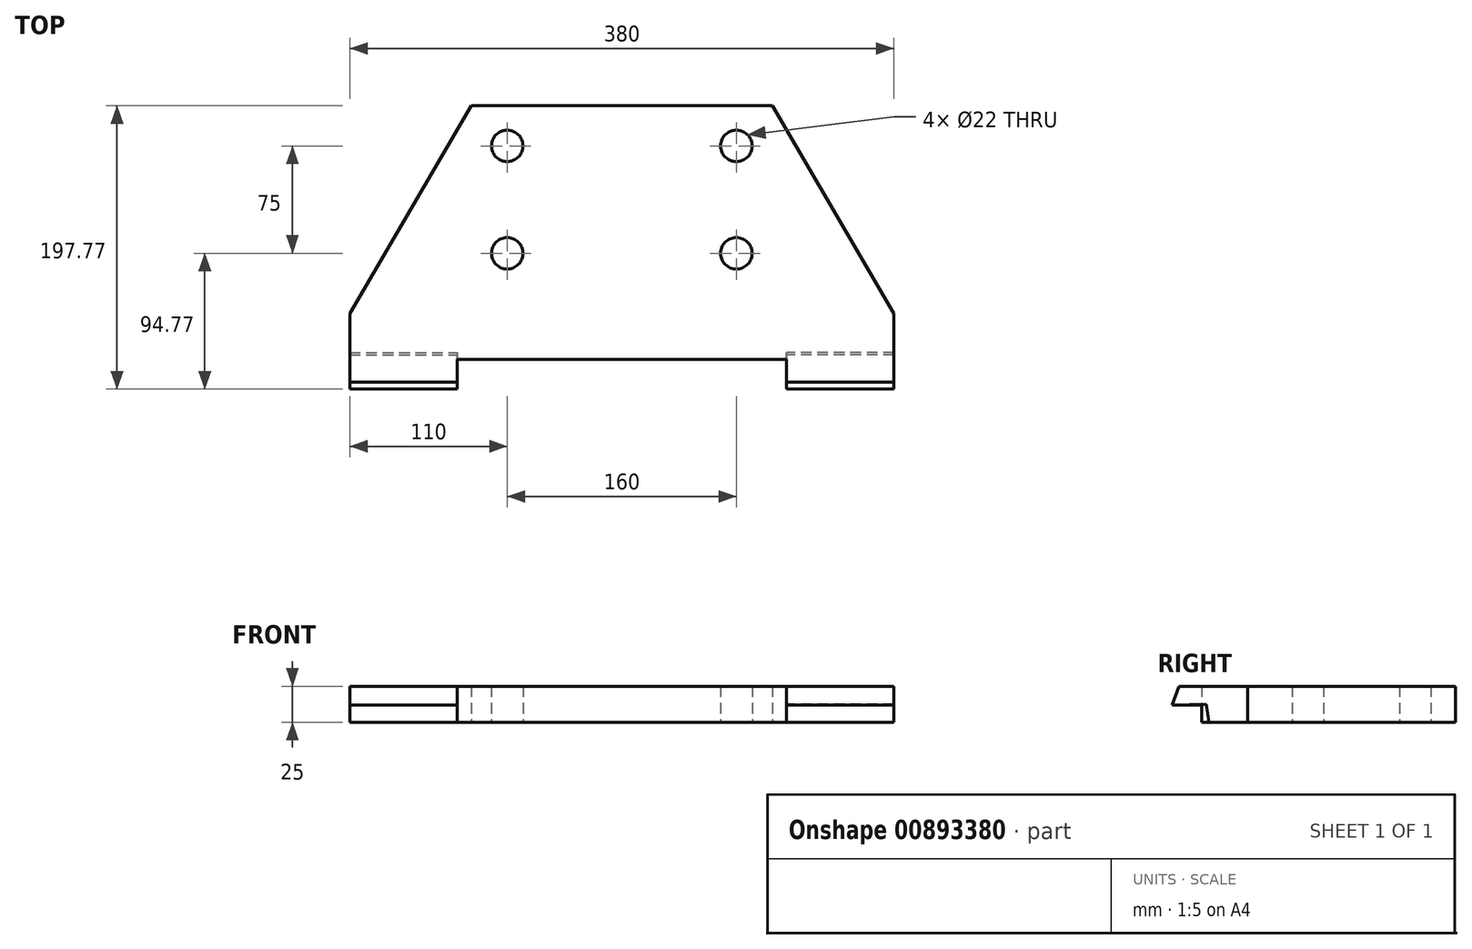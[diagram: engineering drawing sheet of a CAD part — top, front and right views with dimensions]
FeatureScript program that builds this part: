
annotation { "Feature Type Name" : "Feature", "Feature Type Description" : "" }
export const myFeature = defineFeature(function(context is Context, id is Id, definition is map)
    precondition{}
    {
        {
            var Q0;
            Q0=qCreatedBy(makeId("Top.planeOp"),FACE);
            var sketch = newSketch(context, id + "F0", { "sketchPlane" : qUnion([Q0])});
            skLineSegment(sketch, "E0", {"start": v(-105, 101) * mm, "end": v(105, 101) * mm});
            skLineSegment(sketch, "E1", {"start": v(105, 101) * mm, "end": v(190, -44) * mm});
            skLineSegment(sketch, "E2", {"start": v(190, -44) * mm, "end": v(190, -101) * mm});
            skLineSegment(sketch, "E3", {"start": v(190, -101) * mm, "end": v(115, -101) * mm});
            skLineSegment(sketch, "E4", {"start": v(115, -101) * mm, "end": v(115, -76) * mm});
            skLineSegment(sketch, "E5", {"start": v(115, -76) * mm, "end": v(-115, -76) * mm});
            skLineSegment(sketch, "E6", {"start": v(-115, -76) * mm, "end": v(-115, -101) * mm});
            skLineSegment(sketch, "E7", {"start": v(-115, -101) * mm, "end": v(-190, -101) * mm});
            skLineSegment(sketch, "E8", {"start": v(-190, -101) * mm, "end": v(-190, -44) * mm});
            skLineSegment(sketch, "E9", {"start": v(-190, -44) * mm, "end": v(-105, 101) * mm});
            skSolve(sketch);
        }
        {
            var Q0;
            Q0 = qSketchRegion(id + "F0", true);
            extrude(context, id + "F1", {"entities" : qUnion([Q0]), "depth" : 12.5 * mm, "offsetDistance" : 25.4 * mm, "hasSecondDirection" : true, "secondDirectionOppositeDirection" : true, "secondDirectionDepth" : 12.5 * mm});
        }
        {
            var Q0;
            Q0=qCreatedBy(makeId("Right.planeOp"),FACE);
            var sketch = newSketch(context, id + "F2", { "sketchPlane" : qUnion([Q0])});
            skLineSegment(sketch, "E10", {"start": v(-101, 12.5) * mm, "end": v(-92, 12.5) * mm});
            skLineSegment(sketch, "E11", {"start": v(-92, 12.5) * mm, "end": v(-101.17, -12.5) * mm});
            skLineSegment(sketch, "E12", {"start": v(-101.17, -12.5) * mm, "end": v(-101, 12.5) * mm});
            skSolve(sketch);
        }
        {
            var Q0;
            Q0=makeQuery(id+"F2.imprint","IMPRINT",FACE,{"disambiguationData":[TD([[makeQuery(id+"F2.imprint","IMPRINT",EDGE,{"derivedFrom":sQuery(id+"F2.wireOp",EDGE,"E10")}),-1.0]])]});
            extrude(context, id + "F3", {"entities" : qUnion([Q0]), "operationType" : NewBodyOperationType.REMOVE, "depth" : 190 * mm, "offsetDistance" : 25.4 * mm, "hasSecondDirection" : true, "secondDirectionOppositeDirection" : true, "secondDirectionDepth" : 190 * mm});
        }
        {
            var Q0;
            Q0=makeQuery(id+"F1.opExtrude","SWEPT_FACE",FACE,{"disambiguationData":[OSD([sQuery(id+"F0.wireOp",EDGE,"E6")])]});
            var sketch = newSketch(context, id + "F4", { "sketchPlane" : qUnion([Q0])});
            skLineSegment(sketch, "E13", {"start": v(-96.77, -0.5) * mm, "end": v(-72.85, -0.5) * mm});
            skLineSegment(sketch, "E14", {"start": v(-72.85, -0.5) * mm, "end": v(-71.17, -12.5) * mm});
            skLineSegment(sketch, "E15", {"start": v(-71.17, -12.5) * mm, "end": v(-101.17, -12.5) * mm});
            skLineSegment(sketch, "E16", {"start": v(-101.17, -12.5) * mm, "end": v(-96.77, -0.5) * mm});
            skSolve(sketch);
        }
        {
            var Q0;
            Q0 = qSketchRegion(id + "F4", true);
            var Q1;
            Q1=makeQuery(id+"F1.opExtrude","SWEPT_FACE",FACE,{"disambiguationData":[OSD([sQuery(id+"F0.wireOp",EDGE,"E8")])]});
            var Q2;
            Q2=makeQuery(id+"F1.opExtrude","SWEPT_FACE",FACE,{"disambiguationData":[OSD([sQuery(id+"F0.wireOp",EDGE,"E2")])]});
            extrude(context, id + "F5", {"entities" : qUnion([Q0]), "operationType" : NewBodyOperationType.REMOVE, "endBound" : BoundingType.UP_TO_SURFACE, "oppositeDirection" : true, "depth" : 25.4 * mm, "endBoundEntityFace" : qUnion([Q1]), "offsetDistance" : 25.4 * mm});
        }
        {
            var Q0;
            Q0=makeQuery(id+"F1.opExtrude","SWEPT_FACE",FACE,{"disambiguationData":[OSD([sQuery(id+"F0.wireOp",EDGE,"E4")])]});
            var sketch = newSketch(context, id + "F6", { "sketchPlane" : qUnion([Q0])});
            skLineSegment(sketch, "E17", {"start": v(96.77, -0.5) * mm, "end": v(101.17, -12.5) * mm});
            skLineSegment(sketch, "E18", {"start": v(101.17, -12.5) * mm, "end": v(71.17, -12.5) * mm});
            skLineSegment(sketch, "E19", {"start": v(71.17, -12.5) * mm, "end": v(72.92, 0) * mm});
            skLineSegment(sketch, "E20", {"start": v(72.92, 0) * mm, "end": v(96.77, -0.5) * mm});
            skSolve(sketch);
        }
        {
            var Q0;
            Q0 = qSketchRegion(id + "F6", true);
            var Q1;
            Q1=makeQuery(id+"F1.opExtrude","SWEPT_FACE",FACE,{"disambiguationData":[OSD([sQuery(id+"F0.wireOp",EDGE,"E2")])]});
            extrude(context, id + "F7", {"entities" : qUnion([Q0]), "operationType" : NewBodyOperationType.REMOVE, "endBound" : BoundingType.UP_TO_SURFACE, "oppositeDirection" : true, "depth" : 25.4 * mm, "endBoundEntityFace" : qUnion([Q1]), "offsetDistance" : 25.4 * mm});
        }
        {
            var Q0;
            Q0=makeQuery(id+"F1.opExtrude","CAP_FACE",FACE,{"disambiguationData":[OSD([sQuery(id+"F0.wireOp",EDGE,"E0"),sQuery(id+"F0.wireOp",EDGE,"E1"),sQuery(id+"F0.wireOp",EDGE,"E2"),sQuery(id+"F0.wireOp",EDGE,"E3"),sQuery(id+"F0.wireOp",EDGE,"E4"),sQuery(id+"F0.wireOp",EDGE,"E5"),sQuery(id+"F0.wireOp",EDGE,"E6"),sQuery(id+"F0.wireOp",EDGE,"E7"),sQuery(id+"F0.wireOp",EDGE,"E8"),sQuery(id+"F0.wireOp",EDGE,"E9")])],"isStart":true});
            var sketch = newSketch(context, id + "F8", { "sketchPlane" : qUnion([Q0])});
            skCircle(sketch, "E21", {"center": v(-80, -73) * mm, "radius": 11 * mm});
            skCircle(sketch, "E22", {"center": v(-80, 2) * mm, "radius": 11 * mm});
            skCircle(sketch, "E23.MirrorC", {"center": v(80, -73) * mm, "radius": 11 * mm});
            skCircle(sketch, "E24.MirrorC", {"center": v(80, 2) * mm, "radius": 11 * mm});
            skSolve(sketch);
        }
        {
            var Q0;
            Q0 = qSketchRegion(id + "F8", true);
            extrude(context, id + "F9", {"entities" : qUnion([Q0]), "operationType" : NewBodyOperationType.REMOVE, "oppositeDirection" : true, "depth" : 25 * mm, "offsetDistance" : 25 * mm});
        }
    });
